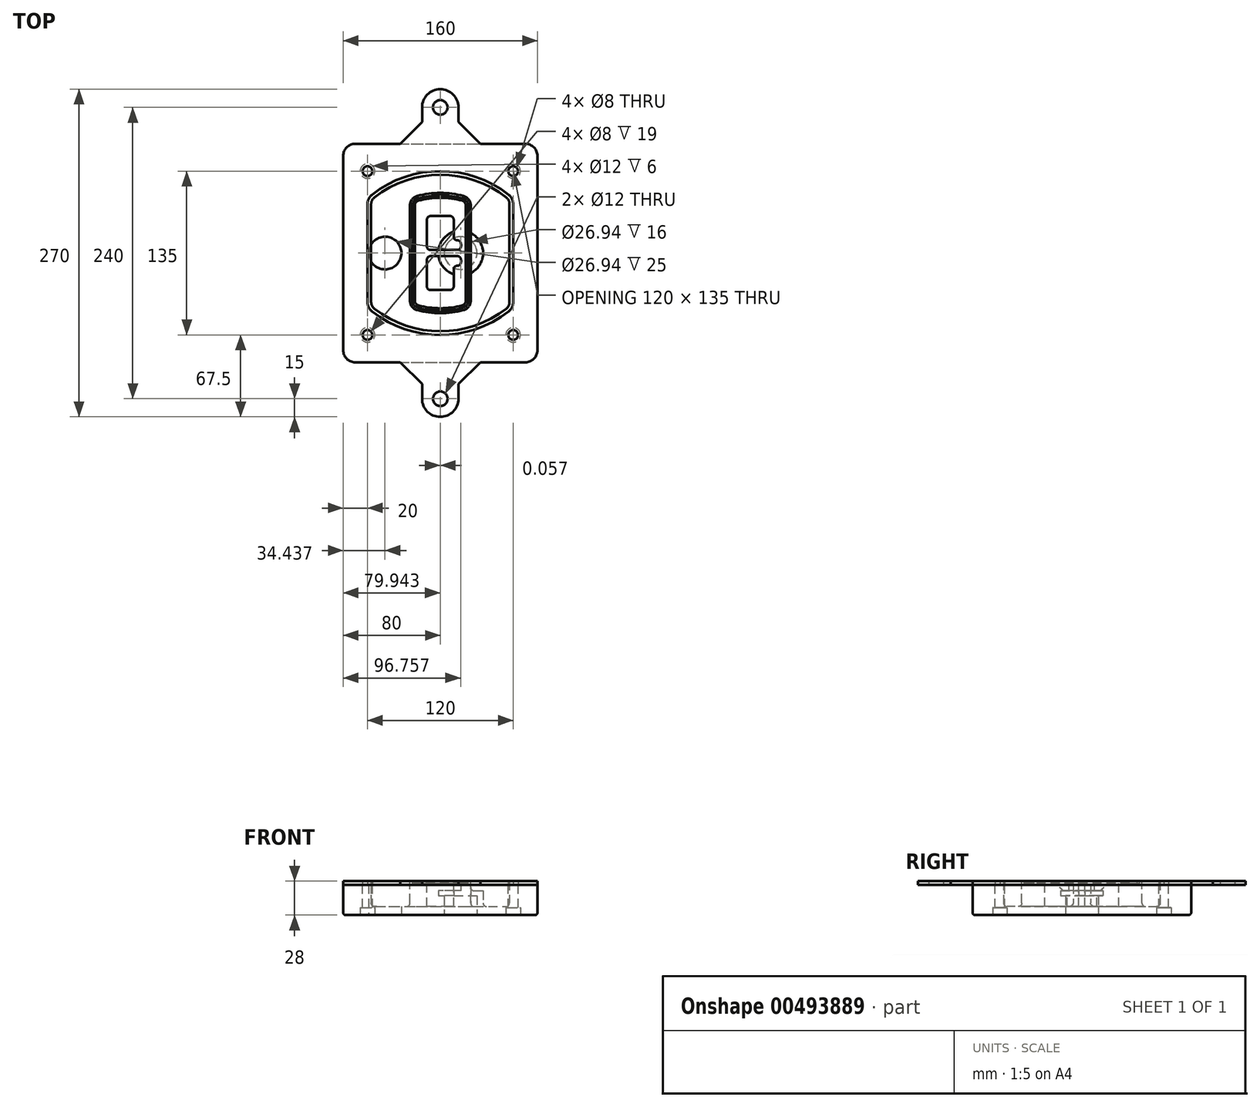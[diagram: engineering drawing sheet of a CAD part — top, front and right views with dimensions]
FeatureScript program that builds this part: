
annotation { "Feature Type Name" : "Feature", "Feature Type Description" : "" }
export const myFeature = defineFeature(function(context is Context, id is Id, definition is map)
    precondition{}
    {
        {
            var Q0;
            Q0=qCreatedBy(makeId("Top.planeOp"),FACE);
            var sketch = newSketch(context, id + "F0", { "sketchPlane" : qUnion([Q0])});
            skPoint(sketch, "E0.rect.middle", {"position": v(0, 0) * mm});
            skLineSegment(sketch, "E1.bottom", {"start": v(-70, -90) * mm, "end": v(70, -90) * mm});
            skLineSegment(sketch, "E1.top", {"start": v(-70, 90) * mm, "end": v(70, 90) * mm});
            skLineSegment(sketch, "E1.left", {"start": v(-80, -80) * mm, "end": v(-80, 80) * mm});
            skLineSegment(sketch, "E1.right", {"start": v(80, -80) * mm, "end": v(80, 80) * mm});
            skLineSegment(sketch, "E2", {"start": v(-80, 90) * mm, "end": v(80, -90) * mm, "construction": true});
            skLineSegment(sketch, "E3", {"start": v(80, 90) * mm, "end": v(-80, -90) * mm, "construction": true});
            skCircle(sketch, "E4", {"center": v(-60, 67.5) * mm, "radius": 4 * mm});
            skCircle(sketch, "E5", {"center": v(60, 67.5) * mm, "radius": 4 * mm});
            skCircle(sketch, "E6", {"center": v(60, -67.5) * mm, "radius": 4 * mm});
            skCircle(sketch, "E7", {"center": v(-60, -67.5) * mm, "radius": 4 * mm});
            skLineSegment(sketch, "E8", {"start": v(-60, 67.5) * mm, "end": v(60, 67.5) * mm, "construction": true});
            skLineSegment(sketch, "E9", {"start": v(60, 67.5) * mm, "end": v(60, -67.5) * mm, "construction": true});
            skLineSegment(sketch, "E10", {"start": v(60, -67.5) * mm, "end": v(-60, -67.5) * mm, "construction": true});
            skLineSegment(sketch, "E11", {"start": v(-60, -67.5) * mm, "end": v(-60, 67.5) * mm, "construction": true});
            skLineSegment(sketch, "E12", {"start": v(-60, 40.3) * mm, "end": v(-60, -40.3) * mm});
            skLineSegment(sketch, "E13", {"start": v(60, 40.3) * mm, "end": v(60, -40.3) * mm});
            skArc(sketch, "E14", {"start": v(56.15, 48.18) * mm, "mid": v(0, 67.5) * mm, "end": v(-56.15, 48.18) * mm});
            skArc(sketch, "E15", {"start": v(-56.15, -48.18) * mm, "mid": v(0, -67.5) * mm, "end": v(56.15, -48.18) * mm});
            skLineSegment(sketch, "E16", {"start": v(-60, 0) * mm, "end": v(60, 0) * mm, "construction": true});
            skPoint(sketch, "E17.visualSharp", {"position": v(-60, -45) * mm});
            skArc(sketch, "E17.filletArc", {"start": v(-60, -40.3) * mm, "mid": v(-58.99, -44.68) * mm, "end": v(-56.15, -48.18) * mm});
            skPoint(sketch, "E18.visualSharp", {"position": v(-60, 45) * mm});
            skArc(sketch, "E18.filletArc", {"start": v(-56.15, 48.18) * mm, "mid": v(-58.99, 44.68) * mm, "end": v(-60, 40.3) * mm});
            skPoint(sketch, "E19.visualSharp", {"position": v(60, 45) * mm});
            skArc(sketch, "E19.filletArc", {"start": v(60, 40.3) * mm, "mid": v(58.99, 44.68) * mm, "end": v(56.15, 48.18) * mm});
            skPoint(sketch, "E20.visualSharp", {"position": v(60, -45) * mm});
            skArc(sketch, "E20.filletArc", {"start": v(56.15, -48.18) * mm, "mid": v(58.99, -44.68) * mm, "end": v(60, -40.3) * mm});
            skPoint(sketch, "E21.visualSharp", {"position": v(-80, 90) * mm});
            skArc(sketch, "E21.filletArc", {"start": v(-70, 90) * mm, "mid": v(-77.07, 87.07) * mm, "end": v(-80, 80) * mm});
            skPoint(sketch, "E22.visualSharp", {"position": v(80, 90) * mm});
            skArc(sketch, "E22.filletArc", {"start": v(80, 80) * mm, "mid": v(77.07, 87.07) * mm, "end": v(70, 90) * mm});
            skPoint(sketch, "E23.visualSharp", {"position": v(80, -90) * mm});
            skArc(sketch, "E23.filletArc", {"start": v(70, -90) * mm, "mid": v(77.07, -87.07) * mm, "end": v(80, -80) * mm});
            skPoint(sketch, "E24.visualSharp", {"position": v(-80, -90) * mm});
            skArc(sketch, "E24.filletArc", {"start": v(-80, -80) * mm, "mid": v(-77.07, -87.07) * mm, "end": v(-70, -90) * mm});
            skArc(sketch, "E25.0", {"start": v(57, 40.3) * mm, "mid": v(56.3, 43.36) * mm, "end": v(54.3, 45.81) * mm});
            skLineSegment(sketch, "E25.1", {"start": v(57, 40.3) * mm, "end": v(57, -40.3) * mm});
            skArc(sketch, "E25.2", {"start": v(54.3, -45.81) * mm, "mid": v(56.3, -43.36) * mm, "end": v(57, -40.3) * mm});
            skArc(sketch, "E25.3", {"start": v(-54.3, -45.81) * mm, "mid": v(0, -64.5) * mm, "end": v(54.3, -45.81) * mm});
            skArc(sketch, "E25.4", {"start": v(-57, -40.3) * mm, "mid": v(-56.3, -43.36) * mm, "end": v(-54.3, -45.81) * mm});
            skArc(sketch, "E25.5", {"start": v(54.3, 45.81) * mm, "mid": v(0, 64.5) * mm, "end": v(-54.3, 45.81) * mm});
            skLineSegment(sketch, "E25.6", {"start": v(-57, 40.3) * mm, "end": v(-57, -40.3) * mm});
            skArc(sketch, "E25.7", {"start": v(-54.3, 45.81) * mm, "mid": v(-56.3, 43.36) * mm, "end": v(-57, 40.3) * mm});
            skArc(sketch, "E26.0", {"start": v(-58.62, 51.33) * mm, "mid": v(-62.58, 46.43) * mm, "end": v(-64, 40.3) * mm});
            skArc(sketch, "E26.1", {"start": v(58.62, 51.33) * mm, "mid": v(0, 71.5) * mm, "end": v(-58.62, 51.33) * mm});
            skArc(sketch, "E26.2", {"start": v(64, 40.3) * mm, "mid": v(62.58, 46.43) * mm, "end": v(58.62, 51.33) * mm});
            skLineSegment(sketch, "E26.3", {"start": v(64, 40.3) * mm, "end": v(64, -40.3) * mm});
            skArc(sketch, "E26.4", {"start": v(58.62, -51.33) * mm, "mid": v(62.58, -46.43) * mm, "end": v(64, -40.3) * mm});
            skLineSegment(sketch, "E26.5", {"start": v(-64, 40.3) * mm, "end": v(-64, -40.3) * mm});
            skArc(sketch, "E26.6", {"start": v(-58.62, -51.33) * mm, "mid": v(0, -71.5) * mm, "end": v(58.62, -51.33) * mm});
            skArc(sketch, "E26.7", {"start": v(-64, -40.3) * mm, "mid": v(-62.58, -46.43) * mm, "end": v(-58.62, -51.33) * mm});
            skSolve(sketch);
        }
        {
            var Q0;
            Q0=makeQuery(id+"F0.imprint","IMPRINT",FACE,{"disambiguationData":[TD([[makeQuery(id+"F0.imprint","IMPRINT",EDGE,{"derivedFrom":sQuery(id+"F0.wireOp",EDGE,"E1.bottom")}),1.0]])]});
            var Q1;
            Q1=makeQuery(id+"F0.imprint","IMPRINT",FACE,{"disambiguationData":[TD([[makeQuery(id+"F0.imprint","IMPRINT",EDGE,{"derivedFrom":sQuery(id+"F0.wireOp",EDGE,"E12")}),1.0]])]});
            var Q2;
            Q2=makeQuery(id+"F0.imprint","IMPRINT",FACE,{"disambiguationData":[TD([[makeQuery(id+"F0.imprint","IMPRINT",EDGE,{"derivedFrom":sQuery(id+"F0.wireOp",EDGE,"E25.0")}),1.0]])]});
            var Q3;
            Q3=makeQuery(id+"F0.imprint","IMPRINT",FACE,{"disambiguationData":[TD([[makeQuery(id+"F0.imprint","IMPRINT",EDGE,{"derivedFrom":sQuery(id+"F0.wireOp",EDGE,"E12")}),-1.0]])]});
            extrude(context, id + "F1", {"entities" : qUnion([Q0, Q1, Q2, Q3]), "oppositeDirection" : true, "depth" : 25 * mm});
        }
        {
            var Q0;
            Q0=makeQuery(id+"F0.imprint","IMPRINT",FACE,{"disambiguationData":[TD([[makeQuery(id+"F0.imprint","IMPRINT",EDGE,{"derivedFrom":sQuery(id+"F0.wireOp",EDGE,"E12")}),1.0]])]});
            extrude(context, id + "F2", {"entities" : qUnion([Q0]), "operationType" : NewBodyOperationType.ADD, "depth" : 3 * mm});
        }
        {
            var Q0;
            Q0=makeQuery(id+"F0.imprint","IMPRINT",FACE,{"disambiguationData":[TD([[makeQuery(id+"F0.imprint","IMPRINT",EDGE,{"derivedFrom":sQuery(id+"F0.wireOp",EDGE,"E25.0")}),1.0]])]});
            extrude(context, id + "F3", {"entities" : qUnion([Q0]), "operationType" : NewBodyOperationType.REMOVE, "oppositeDirection" : true, "depth" : 18 * mm});
        }
        {
            var Q0;
            Q0=makeQuery(id+"F2.opExtrude","CAP_FACE",FACE,{"disambiguationData":[OSD([sQuery(id+"F0.wireOp",EDGE,"E12"),sQuery(id+"F0.wireOp",EDGE,"E13"),sQuery(id+"F0.wireOp",EDGE,"E14"),sQuery(id+"F0.wireOp",EDGE,"E15"),sQuery(id+"F0.wireOp",EDGE,"E17.filletArc"),sQuery(id+"F0.wireOp",EDGE,"E18.filletArc"),sQuery(id+"F0.wireOp",EDGE,"E19.filletArc"),sQuery(id+"F0.wireOp",EDGE,"E20.filletArc"),sQuery(id+"F0.wireOp",EDGE,"E25.0"),sQuery(id+"F0.wireOp",EDGE,"E25.1"),sQuery(id+"F0.wireOp",EDGE,"E25.2"),sQuery(id+"F0.wireOp",EDGE,"E25.3"),sQuery(id+"F0.wireOp",EDGE,"E25.4"),sQuery(id+"F0.wireOp",EDGE,"E25.5"),sQuery(id+"F0.wireOp",EDGE,"E25.6"),sQuery(id+"F0.wireOp",EDGE,"E25.7")])],"isStart":false});
            var sketch = newSketch(context, id + "F4", { "sketchPlane" : qUnion([Q0])});
            skArc(sketch, "E27.0", {"start": v(-19.08, -46.97) * mm, "mid": v(0, -49.5) * mm, "end": v(19.08, -46.97) * mm});
            skArc(sketch, "E28.0", {"start": v(19.08, 46.97) * mm, "mid": v(0, 49.5) * mm, "end": v(-19.08, 46.97) * mm});
            skLineSegment(sketch, "E29", {"start": v(-25, 39.25) * mm, "end": v(-25, -39.25) * mm});
            skLineSegment(sketch, "E30", {"start": v(25, 39.25) * mm, "end": v(25, -39.25) * mm});
            skLineSegment(sketch, "E31", {"start": v(-25, 45.1) * mm, "end": v(25, 45.1) * mm, "construction": true});
            skLineSegment(sketch, "E32", {"start": v(-25, -45.1) * mm, "end": v(25, -45.1) * mm, "construction": true});
            skPoint(sketch, "E33.visualSharp", {"position": v(-25, 45.1) * mm});
            skArc(sketch, "E33.filletArc", {"start": v(-19.08, 46.97) * mm, "mid": v(-23.35, 44.11) * mm, "end": v(-25, 39.25) * mm});
            skPoint(sketch, "E34.visualSharp", {"position": v(25, 45.1) * mm});
            skArc(sketch, "E34.filletArc", {"start": v(25, 39.25) * mm, "mid": v(23.35, 44.11) * mm, "end": v(19.08, 46.97) * mm});
            skPoint(sketch, "E35.visualSharp", {"position": v(25, -45.1) * mm});
            skArc(sketch, "E35.filletArc", {"start": v(19.08, -46.97) * mm, "mid": v(23.35, -44.11) * mm, "end": v(25, -39.25) * mm});
            skPoint(sketch, "E36.visualSharp", {"position": v(-25, -45.1) * mm});
            skArc(sketch, "E36.filletArc", {"start": v(-25, -39.25) * mm, "mid": v(-23.35, -44.11) * mm, "end": v(-19.08, -46.97) * mm});
            skArc(sketch, "E37.0", {"start": v(54.3, 45.81) * mm, "mid": v(0, 64.5) * mm, "end": v(-54.3, 45.81) * mm});
            skArc(sketch, "E37.1", {"start": v(-54.3, 45.81) * mm, "mid": v(-56.3, 43.36) * mm, "end": v(-57, 40.3) * mm});
            skLineSegment(sketch, "E37.2", {"start": v(-57, 40.3) * mm, "end": v(-57, -40.3) * mm});
            skArc(sketch, "E37.3", {"start": v(-57, -40.3) * mm, "mid": v(-56.3, -43.36) * mm, "end": v(-54.3, -45.81) * mm});
            skArc(sketch, "E37.4", {"start": v(-54.3, -45.81) * mm, "mid": v(0, -64.5) * mm, "end": v(54.3, -45.81) * mm});
            skArc(sketch, "E37.5", {"start": v(54.3, -45.81) * mm, "mid": v(56.3, -43.36) * mm, "end": v(57, -40.3) * mm});
            skLineSegment(sketch, "E37.6", {"start": v(57, 40.3) * mm, "end": v(57, -40.3) * mm});
            skArc(sketch, "E37.7", {"start": v(57, 40.3) * mm, "mid": v(56.3, 43.36) * mm, "end": v(54.3, 45.81) * mm});
            skLineSegment(sketch, "E38.0", {"start": v(23, 39.25) * mm, "end": v(23, -39.25) * mm});
            skArc(sketch, "E38.1", {"start": v(18.56, -45.04) * mm, "mid": v(21.76, -42.9) * mm, "end": v(23, -39.25) * mm});
            skArc(sketch, "E38.2", {"start": v(-18.56, -45.04) * mm, "mid": v(0, -47.5) * mm, "end": v(18.56, -45.04) * mm});
            skArc(sketch, "E38.3", {"start": v(-23, -39.25) * mm, "mid": v(-21.76, -42.9) * mm, "end": v(-18.56, -45.04) * mm});
            skLineSegment(sketch, "E38.4", {"start": v(-23, 39.25) * mm, "end": v(-23, -39.25) * mm});
            skArc(sketch, "E38.5", {"start": v(23, 39.25) * mm, "mid": v(21.76, 42.9) * mm, "end": v(18.56, 45.04) * mm});
            skArc(sketch, "E38.6", {"start": v(-18.56, 45.04) * mm, "mid": v(-21.76, 42.9) * mm, "end": v(-23, 39.25) * mm});
            skArc(sketch, "E38.7", {"start": v(18.56, 45.04) * mm, "mid": v(0, 47.5) * mm, "end": v(-18.56, 45.04) * mm});
            skArc(sketch, "E39.0", {"start": v(21, 39.25) * mm, "mid": v(20.18, 41.68) * mm, "end": v(18.04, 43.1) * mm});
            skLineSegment(sketch, "E39.1", {"start": v(21, 39.25) * mm, "end": v(21, -39.25) * mm});
            skArc(sketch, "E39.2", {"start": v(18.04, -43.1) * mm, "mid": v(20.18, -41.68) * mm, "end": v(21, -39.25) * mm});
            skArc(sketch, "E39.3", {"start": v(-18.04, -43.1) * mm, "mid": v(0, -45.5) * mm, "end": v(18.04, -43.1) * mm});
            skArc(sketch, "E39.4", {"start": v(-21, -39.25) * mm, "mid": v(-20.18, -41.68) * mm, "end": v(-18.04, -43.1) * mm});
            skArc(sketch, "E39.5", {"start": v(18.04, 43.1) * mm, "mid": v(0, 45.5) * mm, "end": v(-18.04, 43.1) * mm});
            skLineSegment(sketch, "E39.6", {"start": v(-21, 39.25) * mm, "end": v(-21, -39.25) * mm});
            skArc(sketch, "E39.7", {"start": v(-18.04, 43.1) * mm, "mid": v(-20.18, 41.68) * mm, "end": v(-21, 39.25) * mm});
            skLineSegment(sketch, "E40", {"start": v(-25, 0) * mm, "end": v(25, 0) * mm, "construction": true});
            skLineSegment(sketch, "E41", {"start": v(-11, 5.5) * mm, "end": v(-11, 27.5) * mm});
            skLineSegment(sketch, "E42", {"start": v(-8, 30.5) * mm, "end": v(8, 30.5) * mm});
            skLineSegment(sketch, "E43", {"start": v(11, 27.5) * mm, "end": v(11, 13.5) * mm});
            skLineSegment(sketch, "E44", {"start": v(14, 10.5) * mm, "end": v(14, 10.5) * mm});
            skLineSegment(sketch, "E45", {"start": v(17, 7.5) * mm, "end": v(17, 5.5) * mm});
            skLineSegment(sketch, "E46", {"start": v(14, 2.5) * mm, "end": v(-8, 2.5) * mm});
            skPoint(sketch, "E47.visualSharp", {"position": v(-11, 30.5) * mm});
            skArc(sketch, "E47.filletArc", {"start": v(-8, 30.5) * mm, "mid": v(-10.12, 29.62) * mm, "end": v(-11, 27.5) * mm});
            skPoint(sketch, "E48.visualSharp", {"position": v(11, 30.5) * mm});
            skArc(sketch, "E48.filletArc", {"start": v(11, 27.5) * mm, "mid": v(10.12, 29.62) * mm, "end": v(8, 30.5) * mm});
            skPoint(sketch, "E49.visualSharp", {"position": v(11, 10.5) * mm});
            skArc(sketch, "E49.filletArc", {"start": v(11, 13.5) * mm, "mid": v(11.88, 11.38) * mm, "end": v(14, 10.5) * mm});
            skPoint(sketch, "E50.visualSharp", {"position": v(17, 10.5) * mm});
            skArc(sketch, "E50.filletArc", {"start": v(17, 7.5) * mm, "mid": v(16.12, 9.62) * mm, "end": v(14, 10.5) * mm});
            skPoint(sketch, "E51.visualSharp", {"position": v(17, 2.5) * mm});
            skArc(sketch, "E51.filletArc", {"start": v(14, 2.5) * mm, "mid": v(16.12, 3.38) * mm, "end": v(17, 5.5) * mm});
            skPoint(sketch, "E52.visualSharp", {"position": v(-11, 2.5) * mm});
            skArc(sketch, "E52.filletArc", {"start": v(-11, 5.5) * mm, "mid": v(-10.12, 3.38) * mm, "end": v(-8, 2.5) * mm});
            skLineSegment(sketch, "E53.0.MirrorCS", {"start": v(14, -2.5) * mm, "end": v(-8, -2.5) * mm});
            skArc(sketch, "E54.0.MirrorCS", {"start": v(-11, -5.5) * mm, "mid": v(-10.12, -3.38) * mm, "end": v(-8, -2.5) * mm});
            skLineSegment(sketch, "E55.0.MirrorCS", {"start": v(-11, -5.5) * mm, "end": v(-11, -27.5) * mm});
            skArc(sketch, "E56.0.MirrorCS", {"start": v(-8, -30.5) * mm, "mid": v(-10.12, -29.62) * mm, "end": v(-11, -27.5) * mm});
            skLineSegment(sketch, "E57.0.MirrorCS", {"start": v(-8, -30.5) * mm, "end": v(8, -30.5) * mm});
            skArc(sketch, "E58.0.MirrorCS", {"start": v(11, -27.5) * mm, "mid": v(10.12, -29.62) * mm, "end": v(8, -30.5) * mm});
            skLineSegment(sketch, "E59.0.MirrorCS", {"start": v(11, -27.5) * mm, "end": v(11, -13.5) * mm});
            skArc(sketch, "E60.0.MirrorCS", {"start": v(11, -13.5) * mm, "mid": v(11.88, -11.38) * mm, "end": v(14, -10.5) * mm});
            skArc(sketch, "E61.0.MirrorCS", {"start": v(17, -7.5) * mm, "mid": v(16.12, -9.62) * mm, "end": v(14, -10.5) * mm});
            skLineSegment(sketch, "E62.0.MirrorCS", {"start": v(17, -7.5) * mm, "end": v(17, -5.5) * mm});
            skArc(sketch, "E63.0.MirrorCS", {"start": v(14, -2.5) * mm, "mid": v(16.12, -3.38) * mm, "end": v(17, -5.5) * mm});
            skSolve(sketch);
        }
        {
            var Q0;
            Q0=makeQuery(id+"F4.imprint","IMPRINT",FACE,{"disambiguationData":[TD([[makeQuery(id+"F4.imprint","IMPRINT",EDGE,{"derivedFrom":sQuery(id+"F4.wireOp",EDGE,"E27.0")}),1.0]])]});
            var Q1;
            Q1=makeQuery(id+"F4.imprint","IMPRINT",FACE,{"disambiguationData":[TD([[makeQuery(id+"F4.imprint","IMPRINT",EDGE,{"derivedFrom":sQuery(id+"F4.wireOp",EDGE,"E38.0")}),-1.0]])]});
            var Q2;
            Q2=makeQuery(id+"F4.imprint","IMPRINT",FACE,{"disambiguationData":[TD([[makeQuery(id+"F4.imprint","IMPRINT",EDGE,{"derivedFrom":sQuery(id+"F4.wireOp",EDGE,"E39.0")}),1.0]])]});
            extrude(context, id + "F5", {"entities" : qUnion([Q0, Q1, Q2]), "operationType" : NewBodyOperationType.ADD, "endBound" : BoundingType.UP_TO_NEXT, "oppositeDirection" : true, "depth" : 25 * mm});
        }
        {
            var Q0;
            Q0=makeQuery(id+"F4.imprint","IMPRINT",FACE,{"disambiguationData":[TD([[makeQuery(id+"F4.imprint","IMPRINT",EDGE,{"derivedFrom":sQuery(id+"F4.wireOp",EDGE,"E38.0")}),-1.0]])]});
            extrude(context, id + "F6", {"entities" : qUnion([Q0]), "operationType" : NewBodyOperationType.REMOVE, "oppositeDirection" : true, "depth" : 2 * mm});
        }
        {
            var Q0;
            Q0=makeQuery(id+"F1.opExtrude","CAP_FACE",FACE,{"disambiguationData":[OSD([sQuery(id+"F0.wireOp",EDGE,"E1.bottom"),sQuery(id+"F0.wireOp",EDGE,"E1.top"),sQuery(id+"F0.wireOp",EDGE,"E1.left"),sQuery(id+"F0.wireOp",EDGE,"E1.right"),sQuery(id+"F0.wireOp",EDGE,"E4"),sQuery(id+"F0.wireOp",EDGE,"E5"),sQuery(id+"F0.wireOp",EDGE,"E6"),sQuery(id+"F0.wireOp",EDGE,"E7"),sQuery(id+"F0.wireOp",EDGE,"E21.filletArc"),sQuery(id+"F0.wireOp",EDGE,"E22.filletArc"),sQuery(id+"F0.wireOp",EDGE,"E23.filletArc"),sQuery(id+"F0.wireOp",EDGE,"E24.filletArc")])],"isStart":false});
            var sketch = newSketch(context, id + "F7", { "sketchPlane" : qUnion([Q0])});
            skCircle(sketch, "E64", {"center": v(16.76, 0) * mm, "radius": 13.47 * mm});
            skCircle(sketch, "E65", {"center": v(-45.56, 0) * mm, "radius": 13.47 * mm});
            skLineSegment(sketch, "E66", {"start": v(80, 0) * mm, "end": v(-80, 0) * mm});
            skCircle(sketch, "E67", {"center": v(16.76, 0) * mm, "radius": 18.47 * mm});
            skCircle(sketch, "E68", {"center": v(60, -67.5) * mm, "radius": 6 * mm});
            skCircle(sketch, "E69", {"center": v(-60, -67.5) * mm, "radius": 6 * mm});
            skCircle(sketch, "E70", {"center": v(-60, 67.5) * mm, "radius": 6 * mm});
            skCircle(sketch, "E71", {"center": v(60, 67.5) * mm, "radius": 6 * mm});
            skSolve(sketch);
        }
        {
            var Q0;
            {var subQ1=sQuery(id+"F7.wireOp",EDGE,"E66");var subQ4=sQuery(id+"F7.wireOp",EDGE,"E64");var subQ6=makeQuery(id+"F7.imprint","INTERSECT",VERTEX,{"disambiguationData":[OD(0.0)],"derivedFrom":[subQ4,subQ1]});Q0=makeQuery(id+"F7.imprint","IMPRINT",FACE,{"disambiguationData":[TD([[makeQuery(id+"F7.imprint","IMPRINT",EDGE,{"disambiguationData":[TD([[subQ6,-1.0]])],"derivedFrom":subQ4}),-1.0]])]});}
            var Q1;
            {var subQ0=sQuery(id+"F7.wireOp",EDGE,"E66");var subQ1=sQuery(id+"F7.wireOp",EDGE,"E64");var subQ3=makeQuery(id+"F7.imprint","INTERSECT",VERTEX,{"disambiguationData":[OD(0.0)],"derivedFrom":[subQ1,subQ0]});Q1=makeQuery(id+"F7.imprint","IMPRINT",FACE,{"disambiguationData":[TD([[makeQuery(id+"F7.imprint","IMPRINT",EDGE,{"disambiguationData":[TD([[subQ3,-1.0]])],"derivedFrom":subQ1}),1.0]])]});}
            var Q2;
            {var subQ0=sQuery(id+"F7.wireOp",EDGE,"E66");var subQ1=sQuery(id+"F7.wireOp",EDGE,"E64");var subQ3=makeQuery(id+"F7.imprint","INTERSECT",VERTEX,{"disambiguationData":[OD(0.0)],"derivedFrom":[subQ1,subQ0]});Q2=makeQuery(id+"F7.imprint","IMPRINT",FACE,{"disambiguationData":[TD([[makeQuery(id+"F7.imprint","IMPRINT",EDGE,{"disambiguationData":[TD([[subQ3,1.0]])],"derivedFrom":subQ1}),1.0]])]});}
            var Q3;
            {var subQ1=sQuery(id+"F7.wireOp",EDGE,"E66");var subQ4=sQuery(id+"F7.wireOp",EDGE,"E64");var subQ6=makeQuery(id+"F7.imprint","INTERSECT",VERTEX,{"disambiguationData":[OD(0.0)],"derivedFrom":[subQ4,subQ1]});Q3=makeQuery(id+"F7.imprint","IMPRINT",FACE,{"disambiguationData":[TD([[makeQuery(id+"F7.imprint","IMPRINT",EDGE,{"disambiguationData":[TD([[subQ6,1.0]])],"derivedFrom":subQ4}),-1.0]])]});}
            extrude(context, id + "F8", {"entities" : qUnion([Q0, Q1, Q2, Q3]), "operationType" : NewBodyOperationType.ADD, "oppositeDirection" : true, "depth" : 20 * mm});
        }
        {
            var Q0;
            {var subQ0=sQuery(id+"F7.wireOp",EDGE,"E66");var subQ1=sQuery(id+"F7.wireOp",EDGE,"E64");var subQ3=makeQuery(id+"F7.imprint","INTERSECT",VERTEX,{"disambiguationData":[OD(0.0)],"derivedFrom":[subQ1,subQ0]});Q0=makeQuery(id+"F7.imprint","IMPRINT",FACE,{"disambiguationData":[TD([[makeQuery(id+"F7.imprint","IMPRINT",EDGE,{"disambiguationData":[TD([[subQ3,-1.0]])],"derivedFrom":subQ1}),1.0]])]});}
            var Q1;
            {var subQ0=sQuery(id+"F7.wireOp",EDGE,"E66");var subQ1=sQuery(id+"F7.wireOp",EDGE,"E64");var subQ3=makeQuery(id+"F7.imprint","INTERSECT",VERTEX,{"disambiguationData":[OD(0.0)],"derivedFrom":[subQ1,subQ0]});Q1=makeQuery(id+"F7.imprint","IMPRINT",FACE,{"disambiguationData":[TD([[makeQuery(id+"F7.imprint","IMPRINT",EDGE,{"disambiguationData":[TD([[subQ3,1.0]])],"derivedFrom":subQ1}),1.0]])]});}
            extrude(context, id + "F9", {"entities" : qUnion([Q0, Q1]), "operationType" : NewBodyOperationType.REMOVE, "oppositeDirection" : true, "depth" : 16 * mm});
        }
        {
            var Q0;
            {var subQ0=sQuery(id+"F7.wireOp",EDGE,"E66");var subQ1=sQuery(id+"F7.wireOp",EDGE,"E65");var subQ3=makeQuery(id+"F7.imprint","INTERSECT",VERTEX,{"disambiguationData":[OD(0.0)],"derivedFrom":[subQ1,subQ0]});Q0=makeQuery(id+"F7.imprint","IMPRINT",FACE,{"disambiguationData":[TD([[makeQuery(id+"F7.imprint","IMPRINT",EDGE,{"disambiguationData":[TD([[subQ3,-1.0]])],"derivedFrom":subQ1}),1.0]])]});}
            var Q1;
            {var subQ0=sQuery(id+"F7.wireOp",EDGE,"E66");var subQ1=sQuery(id+"F7.wireOp",EDGE,"E65");var subQ3=makeQuery(id+"F7.imprint","INTERSECT",VERTEX,{"disambiguationData":[OD(0.0)],"derivedFrom":[subQ1,subQ0]});Q1=makeQuery(id+"F7.imprint","IMPRINT",FACE,{"disambiguationData":[TD([[makeQuery(id+"F7.imprint","IMPRINT",EDGE,{"disambiguationData":[TD([[subQ3,1.0]])],"derivedFrom":subQ1}),1.0]])]});}
            extrude(context, id + "F10", {"entities" : qUnion([Q0, Q1]), "operationType" : NewBodyOperationType.REMOVE, "oppositeDirection" : true, "depth" : 25 * mm});
        }
        {
            var Q0;
            Q0=makeQuery(id+"F7.imprint","IMPRINT",FACE,{"disambiguationData":[TD([[makeQuery(id+"F7.imprint","IMPRINT",EDGE,{"derivedFrom":sQuery(id+"F7.wireOp",EDGE,"E68")}),1.0]])]});
            var Q1;
            Q1=makeQuery(id+"F7.imprint","IMPRINT",FACE,{"disambiguationData":[TD([[makeQuery(id+"F7.imprint","IMPRINT",EDGE,{"derivedFrom":makeQuery(id+"F1.opExtrude","CAP_EDGE",EDGE,{"disambiguationData":[OSD([sQuery(id+"F0.wireOp",EDGE,"E5")])],"isStart":false})}),-1.0]])]});
            var Q2;
            Q2=makeQuery(id+"F7.imprint","IMPRINT",FACE,{"disambiguationData":[TD([[makeQuery(id+"F7.imprint","IMPRINT",EDGE,{"derivedFrom":sQuery(id+"F7.wireOp",EDGE,"E69")}),1.0]])]});
            var Q3;
            Q3=makeQuery(id+"F7.imprint","IMPRINT",FACE,{"disambiguationData":[TD([[makeQuery(id+"F7.imprint","IMPRINT",EDGE,{"derivedFrom":makeQuery(id+"F1.opExtrude","CAP_EDGE",EDGE,{"disambiguationData":[OSD([sQuery(id+"F0.wireOp",EDGE,"E4")])],"isStart":false})}),-1.0]])]});
            var Q4;
            Q4=makeQuery(id+"F7.imprint","IMPRINT",FACE,{"disambiguationData":[TD([[makeQuery(id+"F7.imprint","IMPRINT",EDGE,{"derivedFrom":sQuery(id+"F7.wireOp",EDGE,"E70")}),1.0]])]});
            var Q5;
            Q5=makeQuery(id+"F7.imprint","IMPRINT",FACE,{"disambiguationData":[TD([[makeQuery(id+"F7.imprint","IMPRINT",EDGE,{"derivedFrom":makeQuery(id+"F1.opExtrude","CAP_EDGE",EDGE,{"disambiguationData":[OSD([sQuery(id+"F0.wireOp",EDGE,"E7")])],"isStart":false})}),-1.0]])]});
            var Q6;
            Q6=makeQuery(id+"F7.imprint","IMPRINT",FACE,{"disambiguationData":[TD([[makeQuery(id+"F7.imprint","IMPRINT",EDGE,{"derivedFrom":sQuery(id+"F7.wireOp",EDGE,"E71")}),1.0]])]});
            var Q7;
            Q7=makeQuery(id+"F7.imprint","IMPRINT",FACE,{"disambiguationData":[TD([[makeQuery(id+"F7.imprint","IMPRINT",EDGE,{"derivedFrom":makeQuery(id+"F1.opExtrude","CAP_EDGE",EDGE,{"disambiguationData":[OSD([sQuery(id+"F0.wireOp",EDGE,"E6")])],"isStart":false})}),-1.0]])]});
            extrude(context, id + "F11", {"entities" : qUnion([Q0, Q1, Q2, Q3, Q4, Q5, Q6, Q7]), "operationType" : NewBodyOperationType.REMOVE, "oppositeDirection" : true, "depth" : 6 * mm});
        }
        {
            var Q0;
            Q0=makeQuery(id+"F9.boolean.opBoolean","COPY",FACE,{"derivedFrom":makeQuery(id+"F9.opExtrude","CAP_FACE",FACE,{"disambiguationData":[OSD([sQuery(id+"F7.wireOp",EDGE,"E64")])],"isStart":false})});
            var sketch = newSketch(context, id + "F12", { "sketchPlane" : qUnion([Q0])});
            skArc(sketch, "E72.0", {"start": v(11, 17.55) * mm, "mid": v(2.57, 11.82) * mm, "end": v(-1.54, 2.5) * mm});
            skArc(sketch, "E72.1", {"start": v(-1.54, -2.5) * mm, "mid": v(2.57, -11.82) * mm, "end": v(11, -17.55) * mm});
            skLineSegment(sketch, "E73", {"start": v(-1.54, -2.5) * mm, "end": v(14, -2.5) * mm});
            skLineSegment(sketch, "E74.0", {"start": v(14, 2.5) * mm, "end": v(-1.54, 2.5) * mm});
            skArc(sketch, "E74.1", {"start": v(14, 2.5) * mm, "mid": v(16.12, 3.38) * mm, "end": v(17, 5.5) * mm});
            skLineSegment(sketch, "E74.2", {"start": v(17, 7.5) * mm, "end": v(17, 5.5) * mm});
            skArc(sketch, "E74.3", {"start": v(17, 7.5) * mm, "mid": v(16.12, 9.62) * mm, "end": v(14, 10.5) * mm});
            skArc(sketch, "E74.4", {"start": v(11, 13.5) * mm, "mid": v(11.88, 11.38) * mm, "end": v(14, 10.5) * mm});
            skLineSegment(sketch, "E74.5", {"start": v(11, 17.55) * mm, "end": v(11, 13.5) * mm});
            skLineSegment(sketch, "E74.7", {"start": v(14, -2.5) * mm, "end": v(-1.54, -2.5) * mm});
            skArc(sketch, "E74.8", {"start": v(14, -2.5) * mm, "mid": v(16.12, -3.38) * mm, "end": v(17, -5.5) * mm});
            skLineSegment(sketch, "E74.9", {"start": v(17, -7.5) * mm, "end": v(17, -5.5) * mm});
            skArc(sketch, "E74.10", {"start": v(17, -7.5) * mm, "mid": v(16.12, -9.62) * mm, "end": v(14, -10.5) * mm});
            skArc(sketch, "E74.11", {"start": v(11, -13.5) * mm, "mid": v(11.88, -11.38) * mm, "end": v(14, -10.5) * mm});
            skLineSegment(sketch, "E74.12", {"start": v(11, -17.55) * mm, "end": v(11, -13.5) * mm});
            skPoint(sketch, "E75.orphan", {"position": v(11, -27.5) * mm});
            skPoint(sketch, "E76.orphan", {"position": v(-8, -2.5) * mm});
            skPoint(sketch, "E77.orphan", {"position": v(-8, 2.5) * mm});
            skPoint(sketch, "E78.orphan", {"position": v(11, 27.5) * mm});
            skSolve(sketch);
        }
        {
            var Q0;
            {var subQ7=sQuery(id+"F12.wireOp",EDGE,"E72.0");var subQ14=sQuery(id+"F12.wireOp",EDGE,"E72.1");var subQ16=sQuery(id+"F12.wireOp",EDGE,"E74.1");var subQ18=sQuery(id+"F12.wireOp",EDGE,"E74.8");Q0=qUnion([makeQuery(id+"F12.imprint","IMPRINT",FACE,{"disambiguationData":[TD([[makeQuery(id+"F12.imprint","IMPRINT",EDGE,{"derivedFrom":subQ7}),1.0]])]}),makeQuery(id+"F12.imprint","IMPRINT",FACE,{"disambiguationData":[TD([[makeQuery(id+"F12.imprint","IMPRINT",EDGE,{"derivedFrom":subQ14}),1.0]])]}),makeQuery(id+"F12.imprint","IMPRINT",FACE,{"disambiguationData":[TD([[makeQuery(id+"F12.imprint","IMPRINT",EDGE,{"derivedFrom":subQ16}),1.0]])]}),makeQuery(id+"F12.imprint","IMPRINT",FACE,{"disambiguationData":[TD([[makeQuery(id+"F12.imprint","IMPRINT",EDGE,{"derivedFrom":subQ18}),-1.0]])]})]);}
            var Q1;
            Q1=makeQuery(id+"F5.boolean.opBoolean","SPLIT",FACE,{"disambiguationData":[TD([makeQuery(id+"F5.opExtrude","SWEPT_FACE",FACE,{"disambiguationData":[OSD([sQuery(id+"F4.wireOp",EDGE,"E41")])]})])],"derivedFrom":makeQuery(id+"F3.boolean.opBoolean","COPY",FACE,{"derivedFrom":makeQuery(id+"F3.opExtrude","CAP_FACE",FACE,{"disambiguationData":[OSD([sQuery(id+"F0.wireOp",EDGE,"E25.0"),sQuery(id+"F0.wireOp",EDGE,"E25.1"),sQuery(id+"F0.wireOp",EDGE,"E25.2"),sQuery(id+"F0.wireOp",EDGE,"E25.3"),sQuery(id+"F0.wireOp",EDGE,"E25.4"),sQuery(id+"F0.wireOp",EDGE,"E25.5"),sQuery(id+"F0.wireOp",EDGE,"E25.6"),sQuery(id+"F0.wireOp",EDGE,"E25.7")])],"isStart":false})})});
            extrude(context, id + "F13", {"entities" : qUnion([Q0]), "operationType" : NewBodyOperationType.REMOVE, "endBound" : BoundingType.UP_TO_SURFACE, "endBoundEntityFace" : qUnion([Q1]), "depth" : 25 * mm});
        }
        {
            var Q0;
            Q0=makeQuery(id+"F3.boolean.opBoolean","COPY",EDGE,{"derivedFrom":makeQuery(id+"F3.opExtrude","CAP_EDGE",EDGE,{"disambiguationData":[OSD([sQuery(id+"F0.wireOp",EDGE,"E25.6")])],"isStart":false})});
            var Q1;
            Q1=makeQuery(id+"F8.boolean.opBoolean","INTERSECT",EDGE,{"derivedFrom":[makeQuery(id+"F5.opExtrude","SWEPT_FACE",FACE,{"disambiguationData":[OSD([sQuery(id+"F4.wireOp",EDGE,"E30")])]}),makeQuery(id+"F8.opExtrude","CAP_FACE",FACE,{"disambiguationData":[OSD([sQuery(id+"F7.wireOp",EDGE,"E67")])],"isStart":false})]});
            var Q2;
            Q2=makeQuery(id+"F8.boolean.opBoolean","INTERSECT",EDGE,{"disambiguationData":[OD(1.0)],"derivedFrom":[makeQuery(id+"F5.opExtrude","SWEPT_FACE",FACE,{"disambiguationData":[OSD([sQuery(id+"F4.wireOp",EDGE,"E30")])]}),makeQuery(id+"F8.opExtrude","SWEPT_FACE",FACE,{"disambiguationData":[OSD([sQuery(id+"F7.wireOp",EDGE,"E67")])]})]});
            var Q3;
            {var subQ0=sQuery(id+"F4.wireOp",EDGE,"E30");Q3=makeQuery(id+"F8.boolean.opBoolean","SPLIT",EDGE,{"disambiguationData":[TD([makeQuery(id+"F5.opExtrude","SWEPT_FACE",FACE,{"disambiguationData":[OSD([sQuery(id+"F4.wireOp",EDGE,"E35.filletArc")])]})])],"derivedFrom":makeQuery(id+"F5.opExtrude","CAP_EDGE",EDGE,{"disambiguationData":[OSD([subQ0])],"isStart":false})});}
            var Q4;
            {var subQ0=sQuery(id+"F0.wireOp",EDGE,"E25.7");var subQ1=sQuery(id+"F0.wireOp",EDGE,"E25.1");var subQ2=sQuery(id+"F0.wireOp",EDGE,"E25.6");var subQ3=sQuery(id+"F0.wireOp",EDGE,"E25.5");var subQ4=sQuery(id+"F0.wireOp",EDGE,"E25.4");var subQ5=sQuery(id+"F0.wireOp",EDGE,"E25.0");var subQ6=sQuery(id+"F0.wireOp",EDGE,"E25.2");var subQ7=sQuery(id+"F0.wireOp",EDGE,"E25.3");Q4=makeQuery(id+"F8.boolean.opBoolean","INTERSECT",EDGE,{"derivedFrom":[makeQuery(id+"F5.boolean.opBoolean","SPLIT",FACE,{"disambiguationData":[TD([makeQuery(id+"F2.opExtrude","SWEPT_FACE",FACE,{"disambiguationData":[OSD([subQ5])]})])],"derivedFrom":makeQuery(id+"F3.boolean.opBoolean","COPY",FACE,{"derivedFrom":makeQuery(id+"F3.opExtrude","CAP_FACE",FACE,{"disambiguationData":[OSD([subQ5,subQ1,subQ6,subQ7,subQ4,subQ3,subQ2,subQ0])],"isStart":false})})}),makeQuery(id+"F8.opExtrude","SWEPT_FACE",FACE,{"disambiguationData":[OSD([sQuery(id+"F7.wireOp",EDGE,"E67")])]})]});}
            var Q5;
            Q5=makeQuery(id+"F8.boolean.opBoolean","INTERSECT",EDGE,{"disambiguationData":[OD(0.0)],"derivedFrom":[makeQuery(id+"F5.opExtrude","SWEPT_FACE",FACE,{"disambiguationData":[OSD([sQuery(id+"F4.wireOp",EDGE,"E30")])]}),makeQuery(id+"F8.opExtrude","SWEPT_FACE",FACE,{"disambiguationData":[OSD([sQuery(id+"F7.wireOp",EDGE,"E67")])]})]});
            fillet(context, id + "F14", {"entities" : qUnion([Q0, Q1, Q2, Q3, Q4, Q5]), "radius" : 3 * mm, "tangentPropagation" : true, "allowEdgeOverflow" : false});
        }
        {
            var Q0;
            Q0=makeQuery(id+"F1.opExtrude","CAP_EDGE",EDGE,{"disambiguationData":[OSD([sQuery(id+"F0.wireOp",EDGE,"E1.bottom")])],"isStart":false});
            fillet(context, id + "F15", {"entities" : qUnion([Q0]), "radius" : 2 * mm, "tangentPropagation" : true, "allowEdgeOverflow" : false});
        }
        {
            var Q0;
            {var subQ0=sQuery(id+"F0.wireOp",EDGE,"E21.filletArc");var subQ1=sQuery(id+"F0.wireOp",EDGE,"E7");var subQ2=sQuery(id+"F0.wireOp",EDGE,"E6");var subQ3=sQuery(id+"F0.wireOp",EDGE,"E5");var subQ4=sQuery(id+"F0.wireOp",EDGE,"E4");var subQ5=sQuery(id+"F0.wireOp",EDGE,"E22.filletArc");var subQ6=sQuery(id+"F0.wireOp",EDGE,"E1.bottom");var subQ7=sQuery(id+"F0.wireOp",EDGE,"E1.right");var subQ8=sQuery(id+"F0.wireOp",EDGE,"E1.top");var subQ9=sQuery(id+"F0.wireOp",EDGE,"E1.left");var subQ10=sQuery(id+"F0.wireOp",EDGE,"E23.filletArc");var subQ11=sQuery(id+"F0.wireOp",EDGE,"E24.filletArc");Q0=makeQuery(id+"F2.boolean.opBoolean","SPLIT",FACE,{"disambiguationData":[TD([makeQuery(id+"F1.opExtrude","SWEPT_FACE",FACE,{"disambiguationData":[OSD([subQ6])]})])],"derivedFrom":makeQuery(id+"F1.opExtrude","CAP_FACE",FACE,{"disambiguationData":[OSD([subQ6,subQ8,subQ9,subQ7,subQ4,subQ3,subQ2,subQ1,subQ0,subQ5,subQ10,subQ11])],"isStart":true})});}
            var sketch = newSketch(context, id + "F16", { "sketchPlane" : qUnion([Q0])});
            skArc(sketch, "E79", {"start": v(14.94, 120) * mm, "mid": v(-0.06, 135) * mm, "end": v(-15.06, 120) * mm});
            skLineSegment(sketch, "E80", {"start": v(-15.06, 120) * mm, "end": v(-15.06, 108) * mm});
            skLineSegment(sketch, "E81", {"start": v(14.94, 120) * mm, "end": v(14.94, 108) * mm});
            skLineSegment(sketch, "E82", {"start": v(-15.06, 108) * mm, "end": v(-33.06, 90) * mm});
            skLineSegment(sketch, "E83", {"start": v(14.94, 108) * mm, "end": v(32.94, 90) * mm});
            skLineSegment(sketch, "E84", {"start": v(32.94, -90) * mm, "end": v(14.94, -108) * mm});
            skLineSegment(sketch, "E85", {"start": v(14.94, -108) * mm, "end": v(14.94, -120) * mm});
            skLineSegment(sketch, "E86", {"start": v(-33.06, -90) * mm, "end": v(-15.06, -108) * mm});
            skLineSegment(sketch, "E87", {"start": v(-15.06, -108) * mm, "end": v(-15.06, -120) * mm});
            skArc(sketch, "E88", {"start": v(-15.06, -120) * mm, "mid": v(-0.06, -135) * mm, "end": v(14.94, -120) * mm});
            skCircle(sketch, "E89", {"center": v(0, -120) * mm, "radius": 6 * mm});
            skCircle(sketch, "E90", {"center": v(-0.06, 120) * mm, "radius": 6 * mm});
            skLineSegment(sketch, "E91", {"start": v(-0.06, 120) * mm, "end": v(0, 90) * mm, "construction": true});
            skLineSegment(sketch, "E92", {"start": v(0, -120) * mm, "end": v(0, -90) * mm, "construction": true});
            skSolve(sketch);
        }
        {
            var Q0;
            Q0=makeQuery(id+"F16.imprint","IMPRINT",FACE,{"disambiguationData":[TD([[makeQuery(id+"F16.imprint","IMPRINT",EDGE,{"derivedFrom":makeQuery(id+"F1.opExtrude","CAP_EDGE",EDGE,{"disambiguationData":[OSD([sQuery(id+"F0.wireOp",EDGE,"E1.left")])],"isStart":true})}),-1.0]])]});
            var Q1;
            {var subQ1=sQuery(id+"F16.wireOp",EDGE,"E84");Q1=makeQuery(id+"F16.imprint","IMPRINT",FACE,{"disambiguationData":[TD([[makeQuery(id+"F16.imprint","IMPRINT",EDGE,{"derivedFrom":subQ1}),-1.0]])]});}
            var Q2;
            Q2=makeQuery(id+"F16.imprint","IMPRINT",FACE,{"disambiguationData":[TD([[makeQuery(id+"F16.imprint","IMPRINT",EDGE,{"derivedFrom":sQuery(id+"F16.wireOp",EDGE,"E79")}),1.0]])]});
            var Q3;
            Q3=makeQuery(id+"F2.opExtrude","CAP_FACE",FACE,{"disambiguationData":[OSD([sQuery(id+"F0.wireOp",EDGE,"E12"),sQuery(id+"F0.wireOp",EDGE,"E13"),sQuery(id+"F0.wireOp",EDGE,"E14"),sQuery(id+"F0.wireOp",EDGE,"E15"),sQuery(id+"F0.wireOp",EDGE,"E17.filletArc"),sQuery(id+"F0.wireOp",EDGE,"E18.filletArc"),sQuery(id+"F0.wireOp",EDGE,"E19.filletArc"),sQuery(id+"F0.wireOp",EDGE,"E20.filletArc"),sQuery(id+"F0.wireOp",EDGE,"E25.0"),sQuery(id+"F0.wireOp",EDGE,"E25.1"),sQuery(id+"F0.wireOp",EDGE,"E25.2"),sQuery(id+"F0.wireOp",EDGE,"E25.3"),sQuery(id+"F0.wireOp",EDGE,"E25.4"),sQuery(id+"F0.wireOp",EDGE,"E25.5"),sQuery(id+"F0.wireOp",EDGE,"E25.6"),sQuery(id+"F0.wireOp",EDGE,"E25.7")])],"isStart":false});
            extrude(context, id + "F17", {"entities" : qUnion([Q0, Q1, Q2]), "endBound" : BoundingType.UP_TO_SURFACE, "endBoundEntityFace" : qUnion([Q3]), "depth" : 25 * mm});
        }
    });
